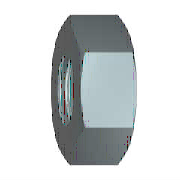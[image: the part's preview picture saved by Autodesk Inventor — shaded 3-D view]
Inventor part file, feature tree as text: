
AUTODESK INVENTOR PART (.ipt)
format: ipt  version: 2023 (Build 270158000, 158)  size: 163,840 bytes
history: native  units: mm (DEFAULTED — no unit token found)
features: sketch x3, other x2, extrude x1, hole x1, plane x1
ambient origin geometry x7: Origin, YZ Plane, XZ Plane, X Axis, Y Axis, Z Axis, Center Point
bodies: Solid1 (feature_tree)
feature tree (8):
  extrude  "Базовый элемент"  Depth=15.011107mm
  other  "Фаска1"
  hole  "Резьба"  [1 undecoded]
  other  "Work Axis1"
  plane  "Work Plane1"
  sketch  "Эскиз1"
  sketch  "Эскиз2"
  sketch  "Эскиз3"
note: 1 required parameter value undecoded (feature->parameter linkage not recoverable at this tier; creation-order binding heuristic only, values carry confidence <= 0.55)
